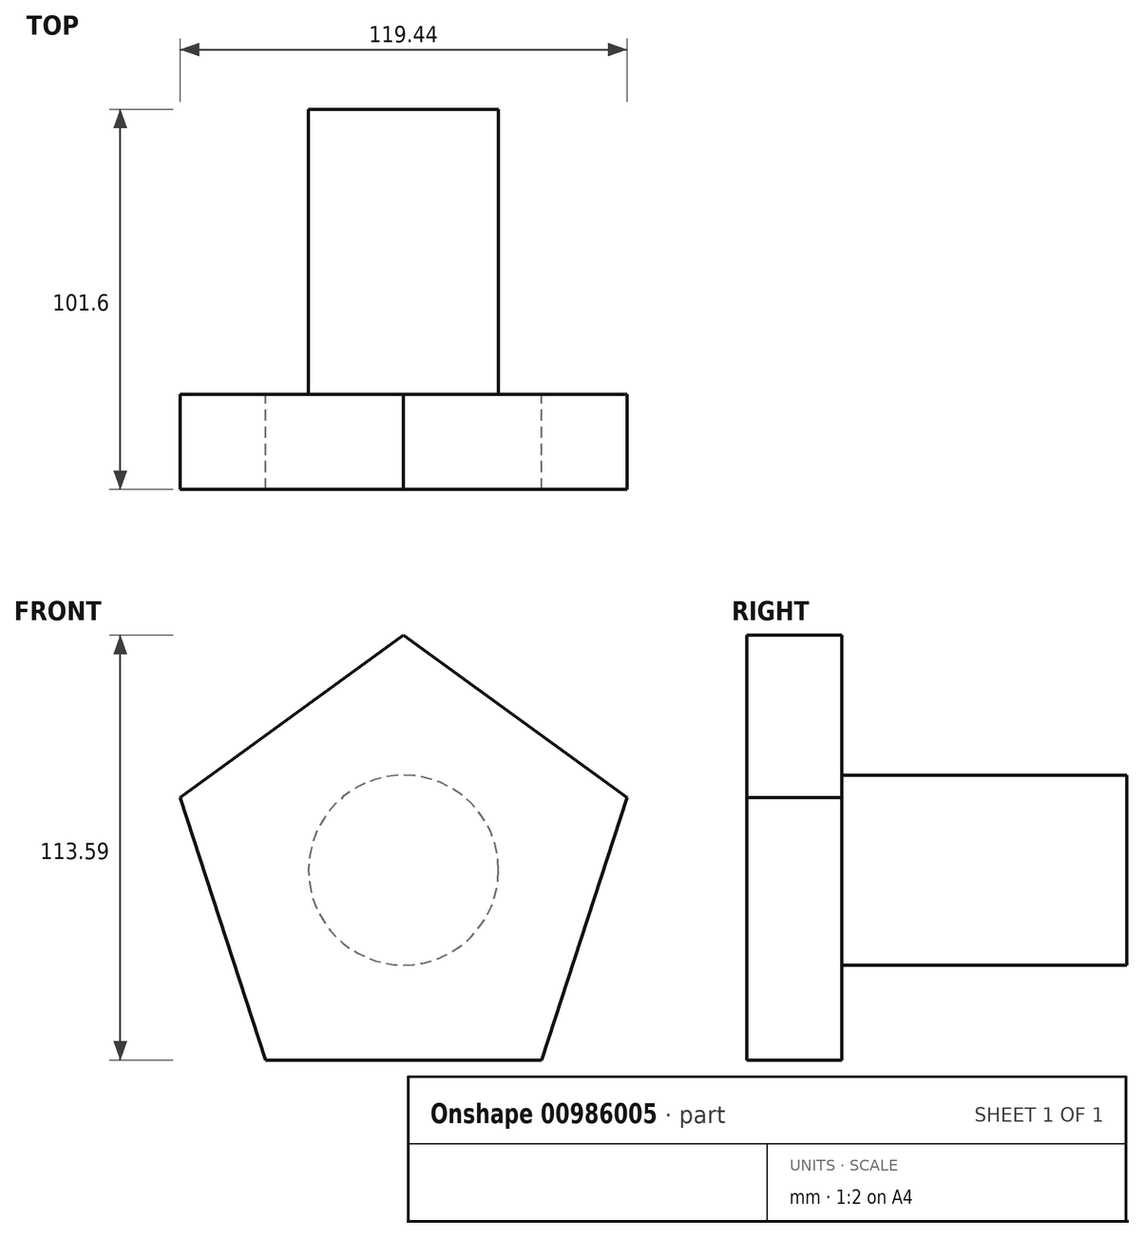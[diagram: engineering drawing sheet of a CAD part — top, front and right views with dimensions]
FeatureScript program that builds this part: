
annotation { "Feature Type Name" : "Feature", "Feature Type Description" : "" }
export const myFeature = defineFeature(function(context is Context, id is Id, definition is map)
    precondition{}
    {
        {
            var Q0;
            Q0=qCreatedBy(makeId("Front.planeOp"),FACE);
            var sketch = newSketch(context, id + "F0", { "sketchPlane" : qUnion([Q0])});
            skCircle(sketch, "E0", {"center": v(0, 0) * mm, "radius": 25.4 * mm});
            skSolve(sketch);
        }
        {
            var Q0;
            Q0 = qSketchRegion(id + "F0", true);
            extrude(context, id + "F1", {"entities" : qUnion([Q0]), "depth" : 76.2 * mm, "offsetDistance" : 25.4 * mm});
        }
        {
            var Q0;
            Q0=makeQuery(id+"F1.opExtrude","CAP_FACE",FACE,{"disambiguationData":[OSD([sQuery(id+"F0.wireOp",EDGE,"E0")])],"isStart":false});
            var sketch = newSketch(context, id + "F2", { "sketchPlane" : qUnion([Q0])});
            skCircle(sketch, "E1.cCircle", {"center": v(0, 0) * mm, "radius": 50.8 * mm, "construction": true});
            skLineSegment(sketch, "E1.0", {"start": v(59.72, 19.4) * mm, "end": v(36.9, -50.8) * mm});
            skLineSegment(sketch, "E1.1", {"start": v(36.9, -50.8) * mm, "end": v(-36.9, -50.8) * mm});
            skLineSegment(sketch, "E1.2", {"start": v(-36.9, -50.8) * mm, "end": v(-59.72, 19.4) * mm});
            skLineSegment(sketch, "E1.3", {"start": v(-59.72, 19.4) * mm, "end": v(0, 62.8) * mm});
            skLineSegment(sketch, "E1.4", {"start": v(0, 62.8) * mm, "end": v(59.72, 19.4) * mm});
            skPoint(sketch, "E1.0.midPoint", {"position": v(48.31, -15.7) * mm});
            skSolve(sketch);
        }
        {
            var Q0;
            Q0 = qSketchRegion(id + "F2", true);
            extrude(context, id + "F3", {"entities" : qUnion([Q0]), "operationType" : NewBodyOperationType.ADD, "depth" : 25.4 * mm, "offsetDistance" : 25.4 * mm});
        }
    });
